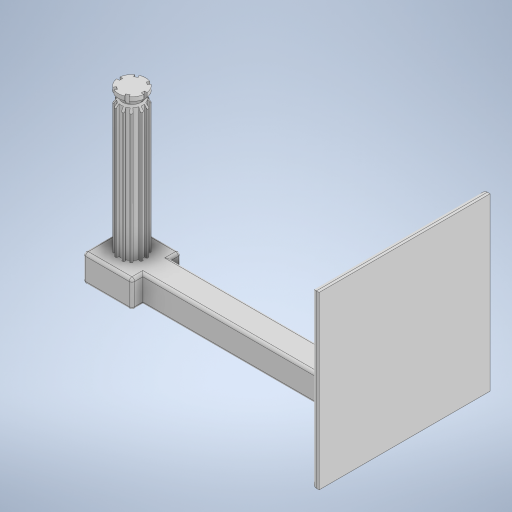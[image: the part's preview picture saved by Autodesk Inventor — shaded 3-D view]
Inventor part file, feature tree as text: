
AUTODESK INVENTOR PART (.ipt)
format: ipt  version: 2024 (Build 280153000, 153)  size: 508,928 bytes
history: native  units: mm
features: sketch x9, extrude x7, fillet x5, chamfer x2, pattern_circular x2, revolve x1
ambient origin geometry x8: Origin, YZ Plane, XZ Plane, XY Plane, X Axis, Y Axis, Z Axis, Center Point
bodies: Volumenkörper1 (feature_tree)
feature tree (26):
  extrude  "Extrusion1"  Depth=10.0mm TaperAngle=0.0deg
  sketch  "Skizze2"  dims[d3=10.0mm d4=100.0mm d5=0.0mm]
  extrude  "Extrusion2"  Depth=10.0mm TaperAngle=0.0deg
  extrude  "Extrusion3"  Depth=10.0mm TaperAngle=0.0deg
  chamfer  "Fasen1"  Distance=10.0mm Angle=45.0deg
  extrude  "Extrusion4"  Depth=3.0mm TaperAngle=0.0deg
  chamfer  "Fasen2"  Distance=4.0mm Angle=45.0deg
  fillet  "Rundung1"  Radius=2.0mm
  fillet  "Rundung2"  Radius=1.5mm
  revolve  "Umdrehung1"
  extrude  "Extrusion5"  Depth=2.0mm
  fillet  "Rundung3"  Radius=2.0mm
  extrude  "Extrusion6"  Depth=1.0mm
  pattern_circular  "Runde Anordnung1"  [2 undecoded]
  extrude  "Extrusion7"  Depth=8.0mm
  pattern_circular  "Runde Anordnung2"  [2 undecoded]
  fillet  "Rundung4"  Radius=0.6mm
  fillet  "Rundung5"  Radius=0.6mm
  sketch  "Skizze1"  dims[d0=10.0mm d1=62.7mm d2=0.0mm]
  sketch  "Skizze3"  dims[d6=3.0mm d7=51.2mm d8=0.0mm d9=10.0mm d10=2.0mm d11=45.0deg]
  sketch  "Skizze4"  dims[d12=62.7mm d13=3.0mm d14=0.0mm d15=4.0mm d16=2.0mm d17=45.0deg d18=2.0mm d20=1.5mm]
  sketch  "Skizze5"  dims[d21=3.5mm d22=2.0mm d23=2.0mm]
  sketch  "Skizze6"  dims[d24=90.0deg d25=1.0mm]
  sketch  "Skizze7"  dims[d26=4.0mm]
  sketch  "Skizze8"  dims[d27=4.0mm]
  sketch  "Skizze9"  dims[d28=10.0mm d29=0.0mm d30=62.7mm d31=1.0mm d32=1.0mm d33=0.6mm d34=0.6mm d35=40.0mm d36=21.35mm d37=0.0mm d38=0.0mm d39=60.0mm d40=360.0deg d42=1.0mm d43=28.0mm d44=21.35mm d45=0.0mm d46=0.0mm d47=60.0mm d48=360.0deg d50=0.29mm d51=1.0mm d52=0.29mm d53=8.0mm d54=0.0mm d55=0.0mm]
note: 4 required parameter values undecoded (feature->parameter linkage not recoverable at this tier; creation-order binding heuristic only, values carry confidence <= 0.55)
